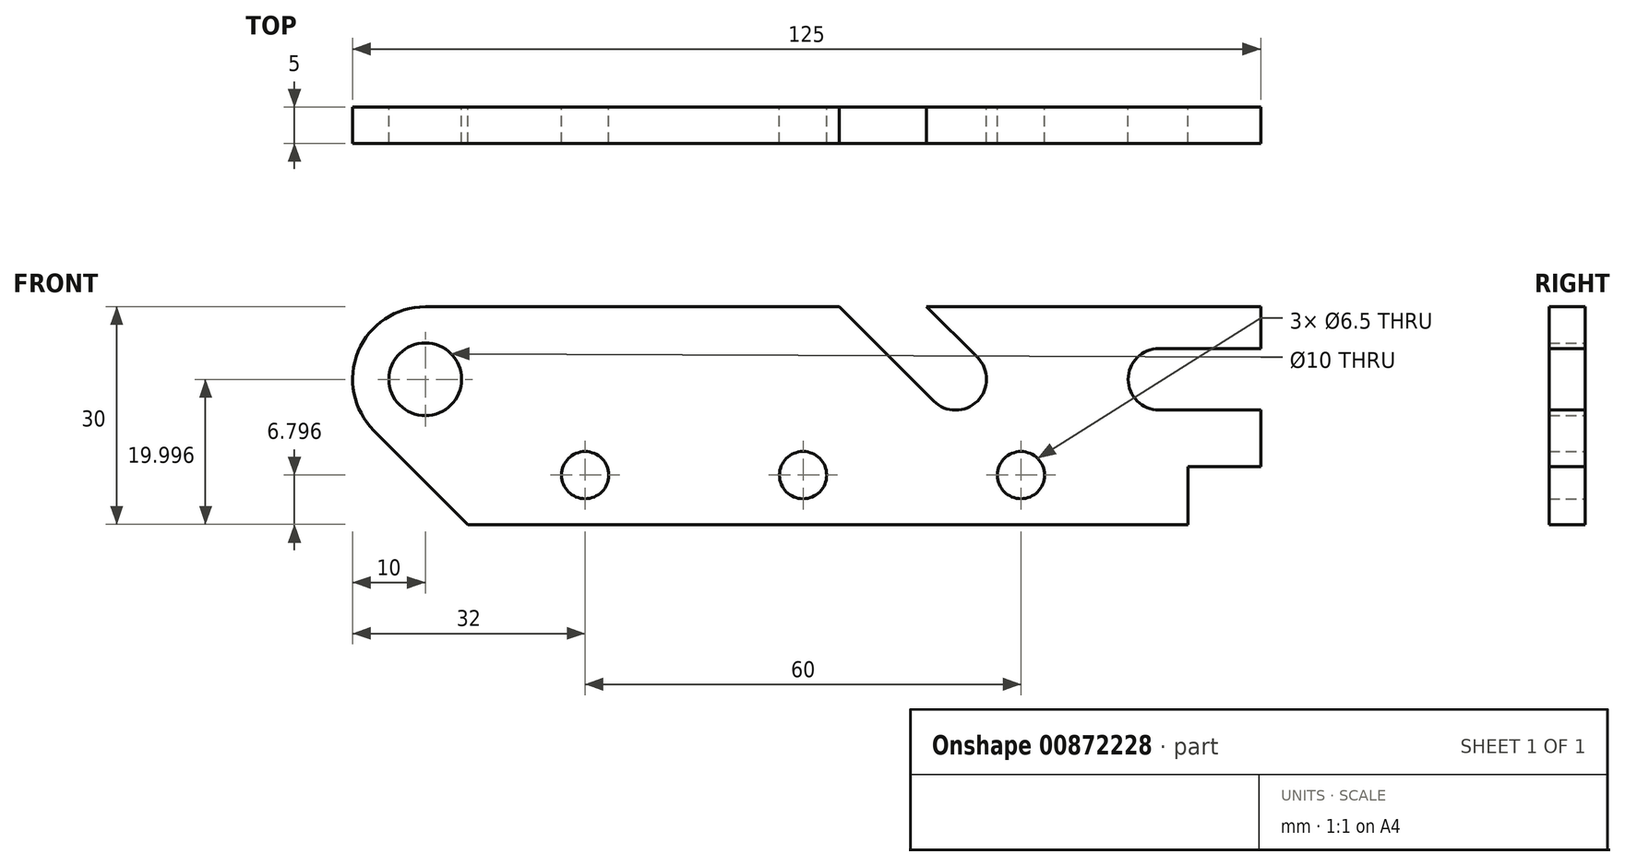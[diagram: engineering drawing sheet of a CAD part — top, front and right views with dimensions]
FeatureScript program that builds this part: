
annotation { "Feature Type Name" : "Feature", "Feature Type Description" : "" }
export const myFeature = defineFeature(function(context is Context, id is Id, definition is map)
    precondition{}
    {
        {
            var Q0;
            Q0=qCreatedBy(makeId("Front.planeOp"),FACE);
            var sketch = newSketch(context, id + "F0", { "sketchPlane" : qUnion([Q0])});
            skPoint(sketch, "E0", {"position": v(-63.18, 13.65) * mm});
            skCircle(sketch, "E1", {"center": v(-63.18, 13.65) * mm, "radius": 5 * mm});
            skArc(sketch, "E2", {"start": v(-63.18, 23.65) * mm, "mid": v(-72.42, 17.47) * mm, "end": v(-70.25, 6.57) * mm});
            skLineSegment(sketch, "E3", {"start": v(-63.18, 23.65) * mm, "end": v(-6.2, 23.65) * mm});
            skLineSegment(sketch, "E4", {"start": v(51.82, 23.65) * mm, "end": v(51.82, 17.9) * mm});
            skPoint(sketch, "E5", {"position": v(18.82, 0.45) * mm});
            skPoint(sketch, "E6", {"position": v(-11.18, 0.45) * mm});
            skPoint(sketch, "E7", {"position": v(-41.18, 0.45) * mm});
            skLineSegment(sketch, "E8", {"start": v(-70.25, 6.57) * mm, "end": v(-57.32, -6.35) * mm});
            skLineSegment(sketch, "E9", {"start": v(41.82, -6.35) * mm, "end": v(-57.32, -6.35) * mm});
            skPoint(sketch, "E10", {"position": v(37.82, 13.65) * mm});
            skArc(sketch, "E11", {"start": v(37.82, 17.9) * mm, "mid": v(33.57, 13.65) * mm, "end": v(37.82, 9.4) * mm});
            skCircle(sketch, "E12", {"center": v(-41.18, 0.45) * mm, "radius": 3.25 * mm});
            skCircle(sketch, "E13", {"center": v(-11.18, 0.45) * mm, "radius": 3.25 * mm});
            skCircle(sketch, "E14", {"center": v(18.82, 0.45) * mm, "radius": 3.25 * mm});
            skPoint(sketch, "E15", {"position": v(9.82, 13.65) * mm});
            skLineSegment(sketch, "E16", {"start": v(6.82, 10.64) * mm, "end": v(-6.2, 23.65) * mm});
            skLineSegment(sketch, "E17", {"start": v(37.82, 17.9) * mm, "end": v(51.82, 17.9) * mm});
            skLineSegment(sketch, "E18", {"start": v(37.82, 9.4) * mm, "end": v(51.82, 9.4) * mm});
            skPoint(sketch, "E19", {"position": v(51.82, 1.65) * mm});
            skLineSegment(sketch, "E20.bottom", {"start": v(51.82, 1.65) * mm, "end": v(41.82, 1.65) * mm});
            skLineSegment(sketch, "E20.right", {"start": v(41.82, 1.65) * mm, "end": v(41.82, -6.35) * mm});
            skLineSegment(sketch, "E21.trimOffspring", {"start": v(16.08, 23.65) * mm, "end": v(51.82, 23.65) * mm});
            skLineSegment(sketch, "E22.trimOffspring", {"start": v(51.82, 9.4) * mm, "end": v(51.82, 1.65) * mm});
            skPoint(sketch, "E23.orphan", {"position": v(51.82, -6.35) * mm});
            skPoint(sketch, "E24.orphan", {"position": v(0.38, 30.21) * mm});
            skArc(sketch, "E25", {"start": v(6.82, 10.64) * mm, "mid": v(12.83, 10.64) * mm, "end": v(12.83, 16.65) * mm});
            skLineSegment(sketch, "E26", {"start": v(12.83, 16.65) * mm, "end": v(5.83, 23.65) * mm});
            skLineSegment(sketch, "E27", {"start": v(5.83, 23.65) * mm, "end": v(16.65, 23.65) * mm});
            skSolve(sketch);
        }
        {
            var Q0;
            Q0=qSketchRegion(id+"F0",true);
            extrude(context, id + "F1", {"entities" : qUnion([Q0]), "depth" : 5 * mm, "offsetDistance" : 25 * mm});
        }
    });
